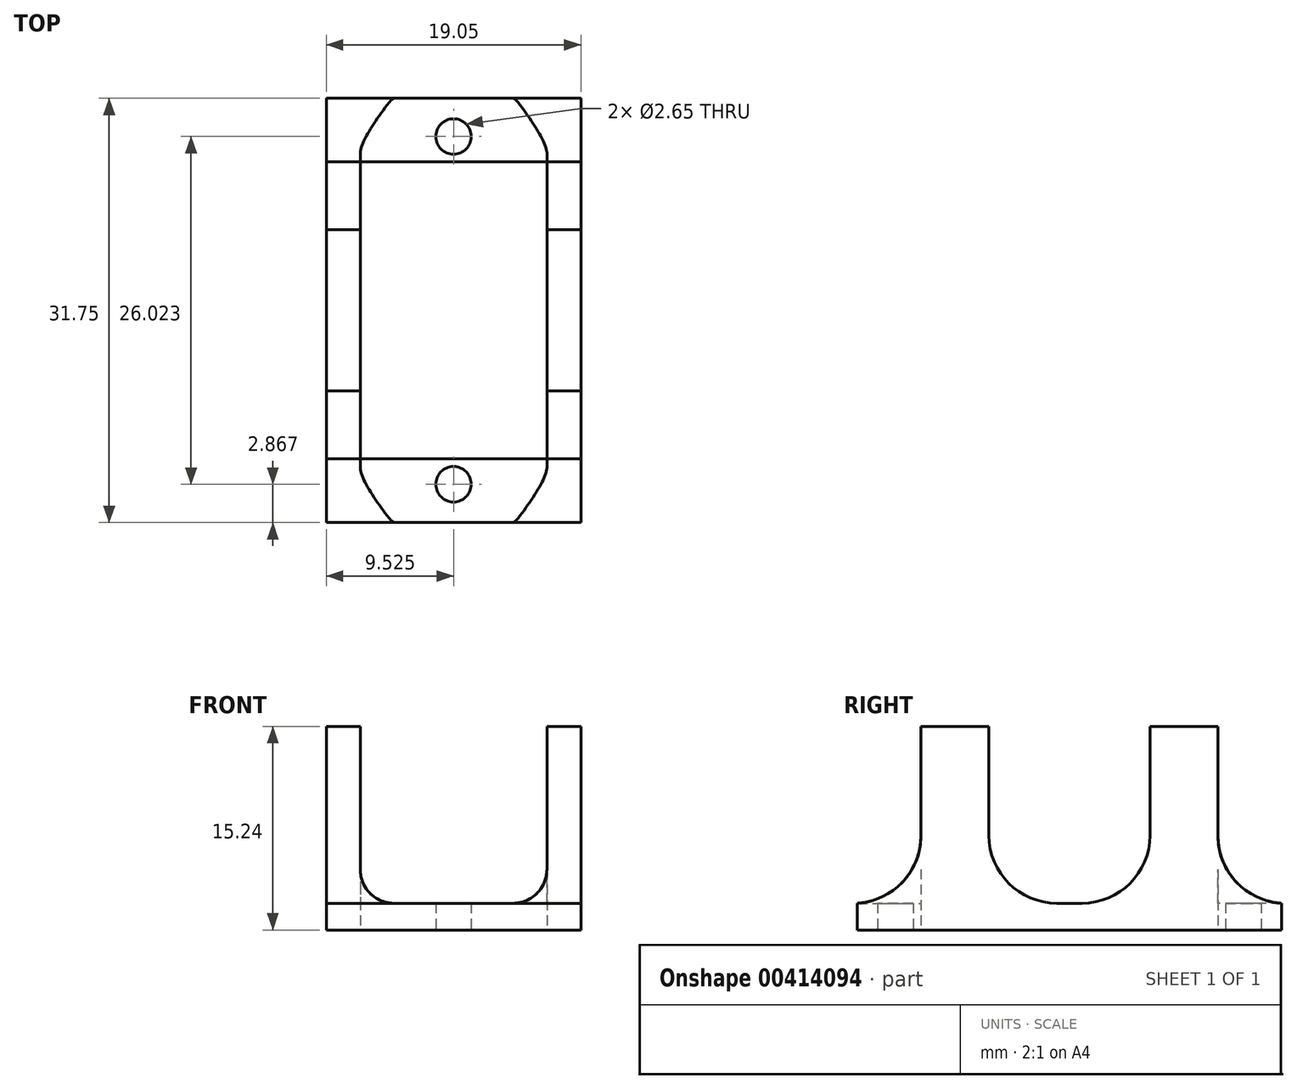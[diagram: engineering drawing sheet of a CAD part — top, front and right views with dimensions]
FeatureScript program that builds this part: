
annotation { "Feature Type Name" : "Feature", "Feature Type Description" : "" }
export const myFeature = defineFeature(function(context is Context, id is Id, definition is map)
    precondition{}
    {
        {
            var Q0;
            Q0=qCreatedBy(makeId("Top.planeOp"),FACE);
            var sketch = newSketch(context, id + "F0", { "sketchPlane" : qUnion([Q0])});
            skCircle(sketch, "E0", {"center": v(37.47, 50.99) * mm, "radius": 1.32 * mm});
            skCircle(sketch, "E1", {"center": v(37.47, 77.01) * mm, "radius": 1.32 * mm});
            skPoint(sketch, "E2", {"position": v(37.47, 64) * mm});
            skLineSegment(sketch, "E3.bottom", {"start": v(47, 48.12) * mm, "end": v(27.94, 48.12) * mm});
            skLineSegment(sketch, "E3.top", {"start": v(47, 79.87) * mm, "end": v(27.94, 79.87) * mm});
            skLineSegment(sketch, "E3.left", {"start": v(47, 48.12) * mm, "end": v(47, 79.87) * mm});
            skLineSegment(sketch, "E3.right", {"start": v(27.94, 48.12) * mm, "end": v(27.94, 79.87) * mm});
            skLineSegment(sketch, "E4.bottom", {"start": v(48.9, 52.9) * mm, "end": v(26.04, 52.9) * mm});
            skLineSegment(sketch, "E4.top", {"start": v(48.9, 75.1) * mm, "end": v(26.04, 75.1) * mm});
            skPoint(sketch, "E5.startSnap0", {"position": v(37.47, 52.9) * mm});
            skPoint(sketch, "E5.endSnap0", {"position": v(37.47, 75.1) * mm});
            skPoint(sketch, "E6.trimOffspring.end.orphan", {"position": v(37.47, 75.69) * mm});
            skPoint(sketch, "E5.start.orphan", {"position": v(37.47, 52.31) * mm});
            skLineSegment(sketch, "E7.bottom", {"start": v(44.45, 52.9) * mm, "end": v(30.48, 52.9) * mm});
            skLineSegment(sketch, "E7.top", {"start": v(44.45, 75.1) * mm, "end": v(30.48, 75.1) * mm});
            skLineSegment(sketch, "E7.left", {"start": v(44.45, 52.9) * mm, "end": v(44.45, 75.1) * mm});
            skLineSegment(sketch, "E7.right", {"start": v(30.48, 52.9) * mm, "end": v(30.48, 75.1) * mm});
            skSolve(sketch);
        }
        {
            var Q0;
            Q0=makeQuery(id+"F0.imprint","IMPRINT",FACE,{"disambiguationData":[TD([[makeQuery(id+"F0.imprint","IMPRINT",EDGE,{"derivedFrom":sQuery(id+"F0.wireOp",EDGE,"E0")}),-1.0]])]});
            var Q1;
            Q1=makeQuery(id+"F0.imprint","IMPRINT",FACE,{"disambiguationData":[TD([[makeQuery(id+"F0.imprint","IMPRINT",EDGE,{"derivedFrom":sQuery(id+"F0.wireOp",EDGE,"E1")}),-1.0]])]});
            var Q2;
            {var subQ5=sQuery(id+"F0.wireOp",EDGE,"E7.right");Q2=makeQuery(id+"F0.imprint","IMPRINT",FACE,{"disambiguationData":[TD([[makeQuery(id+"F0.imprint","IMPRINT",EDGE,{"derivedFrom":subQ5}),1.0]])]});}
            var Q3;
            {var subQ5=sQuery(id+"F0.wireOp",EDGE,"E7.left");Q3=makeQuery(id+"F0.imprint","IMPRINT",FACE,{"disambiguationData":[TD([[makeQuery(id+"F0.imprint","IMPRINT",EDGE,{"derivedFrom":subQ5}),-1.0]])]});}
            extrude(context, id + "F1", {"entities" : qUnion([Q0, Q1, Q2, Q3]), "depth" : 2 * mm});
        }
        {
            var Q0;
            Q0=makeQuery(id+"F1.opExtrude","CAP_FACE",FACE,{"disambiguationData":[OSD([sQuery(id+"F0.wireOp",EDGE,"E0"),sQuery(id+"F0.wireOp",EDGE,"E1"),sQuery(id+"F0.wireOp",EDGE,"E3.bottom"),sQuery(id+"F0.wireOp",EDGE,"E3.top"),sQuery(id+"F0.wireOp",EDGE,"E3.left"),sQuery(id+"F0.wireOp",EDGE,"E3.right"),sQuery(id+"F0.wireOp",EDGE,"E7.bottom"),sQuery(id+"F0.wireOp",EDGE,"E7.top"),sQuery(id+"F0.wireOp",EDGE,"E7.left"),sQuery(id+"F0.wireOp",EDGE,"E7.right")])],"isStart":true});
            var sketch = newSketch(context, id + "F2", { "sketchPlane" : qUnion([Q0])});
            skLineSegment(sketch, "E8.bottom", {"start": v(30.48, -52.9) * mm, "end": v(27.94, -52.9) * mm});
            skLineSegment(sketch, "E8.top", {"start": v(30.48, -57.97) * mm, "end": v(27.94, -57.97) * mm});
            skLineSegment(sketch, "E8.left", {"start": v(30.48, -52.9) * mm, "end": v(30.48, -57.97) * mm});
            skLineSegment(sketch, "E8.right", {"start": v(27.94, -52.9) * mm, "end": v(27.94, -57.97) * mm});
            skLineSegment(sketch, "E9.bottom", {"start": v(30.48, -75.1) * mm, "end": v(27.94, -75.1) * mm});
            skLineSegment(sketch, "E9.top", {"start": v(30.48, -70.02) * mm, "end": v(27.94, -70.02) * mm});
            skLineSegment(sketch, "E9.left", {"start": v(30.48, -75.1) * mm, "end": v(30.48, -70.02) * mm});
            skLineSegment(sketch, "E9.right", {"start": v(27.94, -75.1) * mm, "end": v(27.94, -70.02) * mm});
            skLineSegment(sketch, "E10.bottom", {"start": v(44.45, -75.1) * mm, "end": v(47, -75.1) * mm});
            skLineSegment(sketch, "E10.top", {"start": v(44.45, -70.02) * mm, "end": v(47, -70.02) * mm});
            skLineSegment(sketch, "E10.left", {"start": v(44.45, -75.1) * mm, "end": v(44.45, -70.02) * mm});
            skLineSegment(sketch, "E10.right", {"start": v(47, -75.1) * mm, "end": v(47, -70.02) * mm});
            skLineSegment(sketch, "E11.bottom", {"start": v(44.45, -52.9) * mm, "end": v(47, -52.9) * mm});
            skLineSegment(sketch, "E11.top", {"start": v(44.45, -57.97) * mm, "end": v(47, -57.97) * mm});
            skLineSegment(sketch, "E11.left", {"start": v(44.45, -52.9) * mm, "end": v(44.45, -57.97) * mm});
            skLineSegment(sketch, "E11.right", {"start": v(47, -52.9) * mm, "end": v(47, -57.97) * mm});
            skSolve(sketch);
        }
        {
            var Q0;
            Q0=makeQuery(id+"F2.imprint","IMPRINT",FACE,{"disambiguationData":[TD([[makeQuery(id+"F2.imprint","IMPRINT",EDGE,{"derivedFrom":sQuery(id+"F2.wireOp",EDGE,"E8.bottom")}),1.0]])]});
            var Q1;
            Q1=makeQuery(id+"F2.imprint","IMPRINT",FACE,{"disambiguationData":[TD([[makeQuery(id+"F2.imprint","IMPRINT",EDGE,{"derivedFrom":sQuery(id+"F2.wireOp",EDGE,"E9.bottom")}),-1.0]])]});
            var Q2;
            Q2=makeQuery(id+"F2.imprint","IMPRINT",FACE,{"disambiguationData":[TD([[makeQuery(id+"F2.imprint","IMPRINT",EDGE,{"derivedFrom":sQuery(id+"F2.wireOp",EDGE,"E10.bottom")}),1.0]])]});
            var Q3;
            Q3=makeQuery(id+"F2.imprint","IMPRINT",FACE,{"disambiguationData":[TD([[makeQuery(id+"F2.imprint","IMPRINT",EDGE,{"derivedFrom":sQuery(id+"F2.wireOp",EDGE,"E11.bottom")}),-1.0]])]});
            extrude(context, id + "F3", {"entities" : qUnion([Q0, Q1, Q2, Q3]), "operationType" : NewBodyOperationType.ADD, "oppositeDirection" : true, "depth" : 15.24 * mm});
        }
        {
            var Q0;
            Q0=makeQuery(id+"F3.boolean.opBoolean","INTERSECT",EDGE,{"derivedFrom":[makeQuery(id+"F1.opExtrude","CAP_FACE",FACE,{"disambiguationData":[OSD([sQuery(id+"F0.wireOp",EDGE,"E0"),sQuery(id+"F0.wireOp",EDGE,"E1"),sQuery(id+"F0.wireOp",EDGE,"E3.bottom"),sQuery(id+"F0.wireOp",EDGE,"E3.top"),sQuery(id+"F0.wireOp",EDGE,"E3.left"),sQuery(id+"F0.wireOp",EDGE,"E3.right"),sQuery(id+"F0.wireOp",EDGE,"E7.bottom"),sQuery(id+"F0.wireOp",EDGE,"E7.top"),sQuery(id+"F0.wireOp",EDGE,"E7.left"),sQuery(id+"F0.wireOp",EDGE,"E7.right")])],"isStart":false}),makeQuery(id+"F3.opExtrude","SWEPT_FACE",FACE,{"disambiguationData":[OSD([sQuery(id+"F2.wireOp",EDGE,"E8.bottom")])]})]});
            var Q1;
            Q1=makeQuery(id+"F3.boolean.opBoolean","INTERSECT",EDGE,{"derivedFrom":[makeQuery(id+"F1.opExtrude","CAP_FACE",FACE,{"disambiguationData":[OSD([sQuery(id+"F0.wireOp",EDGE,"E0"),sQuery(id+"F0.wireOp",EDGE,"E1"),sQuery(id+"F0.wireOp",EDGE,"E3.bottom"),sQuery(id+"F0.wireOp",EDGE,"E3.top"),sQuery(id+"F0.wireOp",EDGE,"E3.left"),sQuery(id+"F0.wireOp",EDGE,"E3.right"),sQuery(id+"F0.wireOp",EDGE,"E7.bottom"),sQuery(id+"F0.wireOp",EDGE,"E7.top"),sQuery(id+"F0.wireOp",EDGE,"E7.left"),sQuery(id+"F0.wireOp",EDGE,"E7.right")])],"isStart":false}),makeQuery(id+"F3.opExtrude","SWEPT_FACE",FACE,{"disambiguationData":[OSD([sQuery(id+"F2.wireOp",EDGE,"E9.top")])]})]});
            var Q2;
            Q2=makeQuery(id+"F3.boolean.opBoolean","INTERSECT",EDGE,{"derivedFrom":[makeQuery(id+"F1.opExtrude","CAP_FACE",FACE,{"disambiguationData":[OSD([sQuery(id+"F0.wireOp",EDGE,"E0"),sQuery(id+"F0.wireOp",EDGE,"E1"),sQuery(id+"F0.wireOp",EDGE,"E3.bottom"),sQuery(id+"F0.wireOp",EDGE,"E3.top"),sQuery(id+"F0.wireOp",EDGE,"E3.left"),sQuery(id+"F0.wireOp",EDGE,"E3.right"),sQuery(id+"F0.wireOp",EDGE,"E7.bottom"),sQuery(id+"F0.wireOp",EDGE,"E7.top"),sQuery(id+"F0.wireOp",EDGE,"E7.left"),sQuery(id+"F0.wireOp",EDGE,"E7.right")])],"isStart":false}),makeQuery(id+"F3.opExtrude","SWEPT_FACE",FACE,{"disambiguationData":[OSD([sQuery(id+"F2.wireOp",EDGE,"E11.bottom")])]})]});
            var Q3;
            Q3=makeQuery(id+"F3.boolean.opBoolean","INTERSECT",EDGE,{"derivedFrom":[makeQuery(id+"F1.opExtrude","CAP_FACE",FACE,{"disambiguationData":[OSD([sQuery(id+"F0.wireOp",EDGE,"E0"),sQuery(id+"F0.wireOp",EDGE,"E1"),sQuery(id+"F0.wireOp",EDGE,"E3.bottom"),sQuery(id+"F0.wireOp",EDGE,"E3.top"),sQuery(id+"F0.wireOp",EDGE,"E3.left"),sQuery(id+"F0.wireOp",EDGE,"E3.right"),sQuery(id+"F0.wireOp",EDGE,"E7.bottom"),sQuery(id+"F0.wireOp",EDGE,"E7.top"),sQuery(id+"F0.wireOp",EDGE,"E7.left"),sQuery(id+"F0.wireOp",EDGE,"E7.right")])],"isStart":false}),makeQuery(id+"F3.opExtrude","SWEPT_FACE",FACE,{"disambiguationData":[OSD([sQuery(id+"F2.wireOp",EDGE,"E10.top")])]})]});
            var Q4;
            Q4=makeQuery(id+"F3.boolean.opBoolean","INTERSECT",EDGE,{"derivedFrom":[makeQuery(id+"F1.opExtrude","CAP_FACE",FACE,{"disambiguationData":[OSD([sQuery(id+"F0.wireOp",EDGE,"E0"),sQuery(id+"F0.wireOp",EDGE,"E1"),sQuery(id+"F0.wireOp",EDGE,"E3.bottom"),sQuery(id+"F0.wireOp",EDGE,"E3.top"),sQuery(id+"F0.wireOp",EDGE,"E3.left"),sQuery(id+"F0.wireOp",EDGE,"E3.right"),sQuery(id+"F0.wireOp",EDGE,"E7.bottom"),sQuery(id+"F0.wireOp",EDGE,"E7.top"),sQuery(id+"F0.wireOp",EDGE,"E7.left"),sQuery(id+"F0.wireOp",EDGE,"E7.right")])],"isStart":false}),makeQuery(id+"F3.opExtrude","SWEPT_FACE",FACE,{"disambiguationData":[OSD([sQuery(id+"F2.wireOp",EDGE,"E11.top")])]})]});
            var Q5;
            Q5=makeQuery(id+"F3.boolean.opBoolean","INTERSECT",EDGE,{"derivedFrom":[makeQuery(id+"F1.opExtrude","CAP_FACE",FACE,{"disambiguationData":[OSD([sQuery(id+"F0.wireOp",EDGE,"E0"),sQuery(id+"F0.wireOp",EDGE,"E1"),sQuery(id+"F0.wireOp",EDGE,"E3.bottom"),sQuery(id+"F0.wireOp",EDGE,"E3.top"),sQuery(id+"F0.wireOp",EDGE,"E3.left"),sQuery(id+"F0.wireOp",EDGE,"E3.right"),sQuery(id+"F0.wireOp",EDGE,"E7.bottom"),sQuery(id+"F0.wireOp",EDGE,"E7.top"),sQuery(id+"F0.wireOp",EDGE,"E7.left"),sQuery(id+"F0.wireOp",EDGE,"E7.right")])],"isStart":false}),makeQuery(id+"F3.opExtrude","SWEPT_FACE",FACE,{"disambiguationData":[OSD([sQuery(id+"F2.wireOp",EDGE,"E10.bottom")])]})]});
            var Q6;
            Q6=makeQuery(id+"F3.boolean.opBoolean","INTERSECT",EDGE,{"derivedFrom":[makeQuery(id+"F1.opExtrude","CAP_FACE",FACE,{"disambiguationData":[OSD([sQuery(id+"F0.wireOp",EDGE,"E0"),sQuery(id+"F0.wireOp",EDGE,"E1"),sQuery(id+"F0.wireOp",EDGE,"E3.bottom"),sQuery(id+"F0.wireOp",EDGE,"E3.top"),sQuery(id+"F0.wireOp",EDGE,"E3.left"),sQuery(id+"F0.wireOp",EDGE,"E3.right"),sQuery(id+"F0.wireOp",EDGE,"E7.bottom"),sQuery(id+"F0.wireOp",EDGE,"E7.top"),sQuery(id+"F0.wireOp",EDGE,"E7.left"),sQuery(id+"F0.wireOp",EDGE,"E7.right")])],"isStart":false}),makeQuery(id+"F3.opExtrude","SWEPT_FACE",FACE,{"disambiguationData":[OSD([sQuery(id+"F2.wireOp",EDGE,"E9.bottom")])]})]});
            var Q7;
            Q7=makeQuery(id+"F3.boolean.opBoolean","INTERSECT",EDGE,{"derivedFrom":[makeQuery(id+"F1.opExtrude","CAP_FACE",FACE,{"disambiguationData":[OSD([sQuery(id+"F0.wireOp",EDGE,"E0"),sQuery(id+"F0.wireOp",EDGE,"E1"),sQuery(id+"F0.wireOp",EDGE,"E3.bottom"),sQuery(id+"F0.wireOp",EDGE,"E3.top"),sQuery(id+"F0.wireOp",EDGE,"E3.left"),sQuery(id+"F0.wireOp",EDGE,"E3.right"),sQuery(id+"F0.wireOp",EDGE,"E7.bottom"),sQuery(id+"F0.wireOp",EDGE,"E7.top"),sQuery(id+"F0.wireOp",EDGE,"E7.left"),sQuery(id+"F0.wireOp",EDGE,"E7.right")])],"isStart":false}),makeQuery(id+"F3.opExtrude","SWEPT_FACE",FACE,{"disambiguationData":[OSD([sQuery(id+"F2.wireOp",EDGE,"E8.top")])]})]});
            fillet(context, id + "F4", {"entities" : qUnion([Q0, Q1, Q2, Q3, Q4, Q5, Q6, Q7]), "radius" : 5.08 * mm, "tangentPropagation" : true, "allowEdgeOverflow" : false});
        }
        {
            var Q0;
            Q0=makeQuery(id+"F4.opFillet","TWEAK_EDGE",EDGE,{"derivedFrom":[makeQuery(id+"F1.opExtrude","CAP_VERTEX",VERTEX,{"disambiguationData":[OSD([sQuery(id+"F0.wireOp",EDGE,"E4.top"),sQuery(id+"F0.wireOp",EDGE,"E7.top"),sQuery(id+"F0.wireOp",EDGE,"E7.left")])],"isStart":false})]});
            var Q1;
            Q1=makeQuery(id+"F4.opFillet","TWEAK_EDGE",EDGE,{"derivedFrom":[makeQuery(id+"F1.opExtrude","CAP_VERTEX",VERTEX,{"disambiguationData":[OSD([sQuery(id+"F0.wireOp",EDGE,"E4.top"),sQuery(id+"F0.wireOp",EDGE,"E7.top"),sQuery(id+"F0.wireOp",EDGE,"E7.right")])],"isStart":false})]});
            var Q2;
            Q2=makeQuery(id+"F4.opFillet","TWEAK_EDGE",EDGE,{"derivedFrom":[makeQuery(id+"F1.opExtrude","CAP_VERTEX",VERTEX,{"disambiguationData":[OSD([sQuery(id+"F0.wireOp",EDGE,"E4.bottom"),sQuery(id+"F0.wireOp",EDGE,"E7.bottom"),sQuery(id+"F0.wireOp",EDGE,"E7.right")])],"isStart":false})]});
            var Q3;
            Q3=makeQuery(id+"F4.opFillet","TWEAK_EDGE",EDGE,{"derivedFrom":[makeQuery(id+"F1.opExtrude","CAP_VERTEX",VERTEX,{"disambiguationData":[OSD([sQuery(id+"F0.wireOp",EDGE,"E4.bottom"),sQuery(id+"F0.wireOp",EDGE,"E7.bottom"),sQuery(id+"F0.wireOp",EDGE,"E7.left")])],"isStart":false})]});
            fillet(context, id + "F5", {"entities" : qUnion([Q0, Q1, Q2, Q3]), "radius" : 2.54 * mm, "tangentPropagation" : true, "allowEdgeOverflow" : false});
        }
    });
